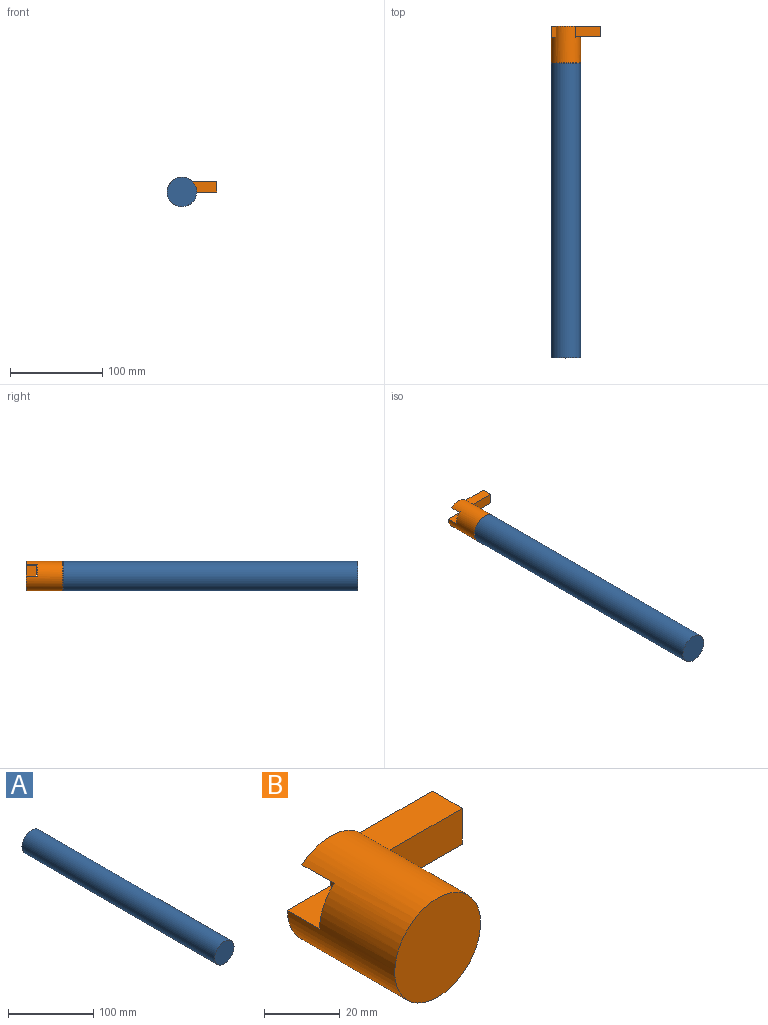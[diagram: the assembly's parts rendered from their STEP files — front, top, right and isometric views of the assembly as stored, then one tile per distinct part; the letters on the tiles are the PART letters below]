
ASSEMBLY  parts=2 mates=1
PART A: 3 faces, bbox 32x320x32 mm
  f0: cylinder r=16mm len=320mm, axis (0,1,0), area 32169.9mm2, adj f1,f2
  f1: plane 32x32mm, normal (0,-1,0), area 804.2mm2, adj f0
  f2: plane 32x32mm, normal (0,1,0), area 804.2mm2, adj f0
PART B: 12 faces, bbox 54x40x32 mm
  f0: plane 32x12mm, normal (0,0,1), area 205.2mm2, adj f1,f4,f6,f9,f11
  f1: cylinder r=16mm len=40mm, axis (0,-1,0), area 3695.6mm2, adj f0,f2,f3,f4,f5,f6,f7
  f2: plane 32x32mm, normal (0,-1,0), area 804.2mm2, adj f1
  f3: plane 21.17x12mm, normal (0,0,-1), area 254mm2, adj f1,f4,f5
  f4: plane 32x12mm, normal (0,1,0), area 344.1mm2, adj f0,f1,f3
  f5: plane 21.17x4mm, normal (0,1,0), area 58mm2, adj f1,f3
  f6: plane 54x27.56mm, normal (0,1,0), area 841.4mm2, adj f0,f1,f7,f8,f10,f11
  f7: plane 22x11.17mm, normal (0,0,-1), area 245.8mm2, adj f1,f6,f9,f10
  f8: plane 38x11.17mm, normal (0,0,1), area 424.6mm2, adj f6,f9,f10,f11
  f9: plane 38x11.56mm, normal (0,-1,0), area 439.3mm2, adj f0,f7,f8,f10,f11
  f10: plane 11.56x11.17mm, normal (1,0,0), area 129.2mm2, adj f6,f7,f8,f9
  f11: plane 11.56x11.17mm, normal (-1,0,0), area 129.2mm2, adj f0,f6,f8,f9
PLACE A t=(-77.52,29,-0.48)mm
PLACE B t=(-77.52,69.49,-0.48)mm
MATE cylindrical A.f0 <-> B.f1  axis (0,1,0) through (-77.52,29,-0.48)mm
